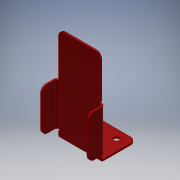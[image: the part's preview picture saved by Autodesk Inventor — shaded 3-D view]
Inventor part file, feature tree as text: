
AUTODESK INVENTOR PART (.ipt)
format: ipt  version: 2018 (Build 220112000, 112)  size: 192,000 bytes
history: native  units: mm
features: other x19, sketch x5, reference x4, hole x1
ambient origin geometry x8: Origin, YZ Plane, XZ Plane, XY Plane, X Axis, Y Axis, Z Axis, Center Point
bodies: Solido1 (feature_tree)
feature tree (29):
  other  "Faccia1"
  other  "Flangia1"
  hole  "Foro1"  [1 undecoded]
  other  "Flangia3"
  other  "Flangia4"
  other  "Arrotondamento angolo1"
  sketch  "Schizzo1"
  other  "Piano1"
  sketch  "Schizzo2"
  other  "Piano2"
  other  "Piega (Bend)1"
  other  "Angolo1"
  sketch  "Schizzo4"
  reference  "Riferimento1"
  reference  "Riferimento2"
  reference  "Riferimento3"
  reference  "Riferimento4"
  sketch  "Schizzo5"
  other  "Piano4"
  other  "Piega (Bend)3"
  other  "Angolo3"
  sketch  "Schizzo6"
  other  "Piano5"
  other  "Piega (Bend)4"
  other  "Angolo4"
  other  "<userpath>\no-brim\Meccanica\Prova Inventor\Assieme 1 - Trasporto.iam"
  other  "Assieme 1 - Trasporto.iam"
  other  "536331 ADN-16-50-A-P-A---(asm_0):1"
  other  "536218 ADN-50-P---(Z):1"
note: 1 required parameter value undecoded (feature->parameter linkage not recoverable at this tier; creation-order binding heuristic only, values carry confidence <= 0.55)
